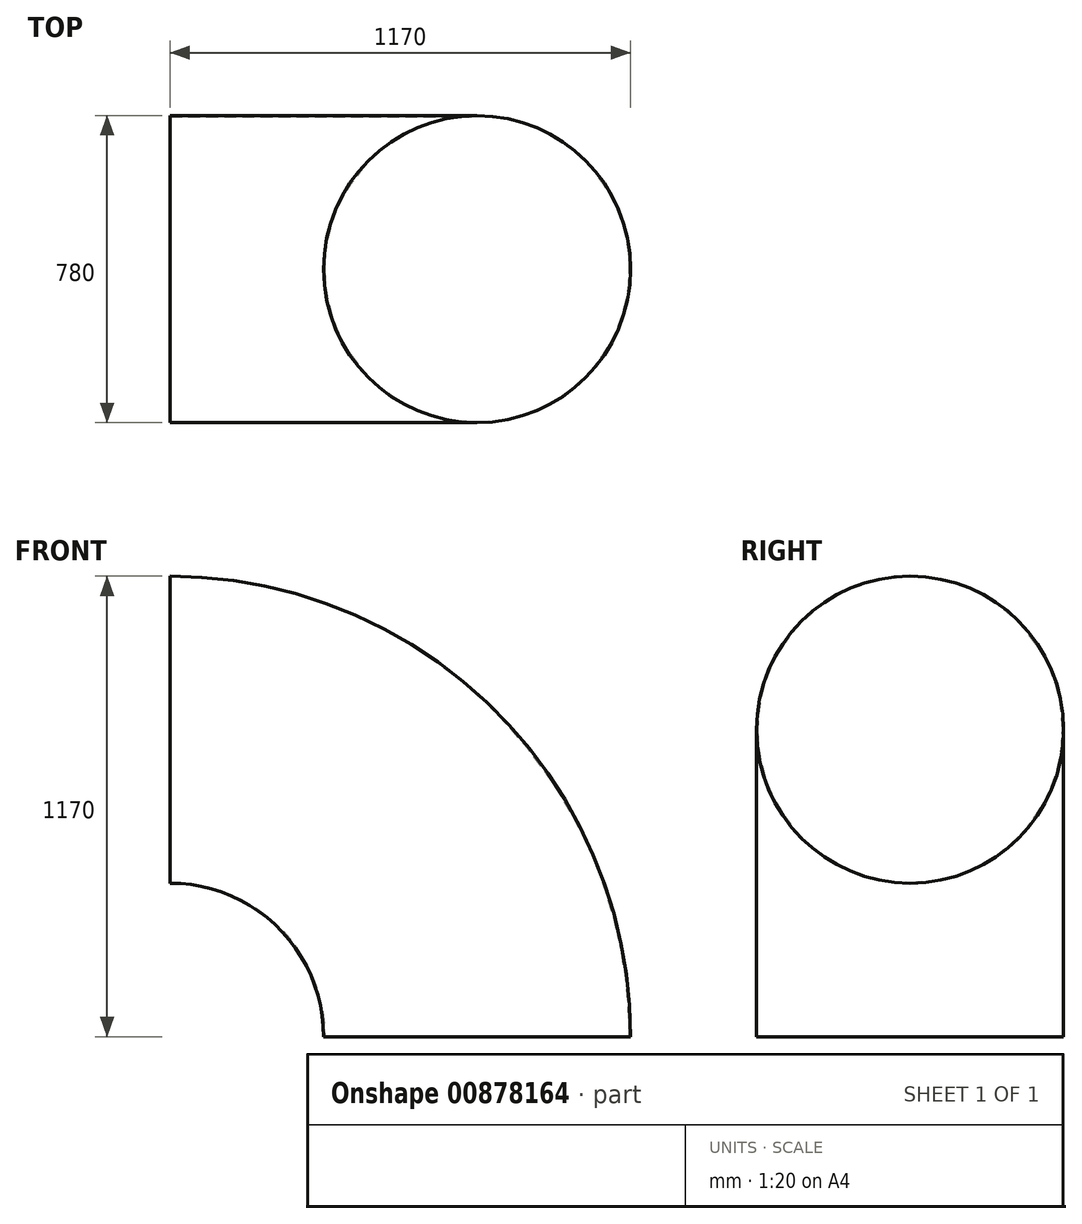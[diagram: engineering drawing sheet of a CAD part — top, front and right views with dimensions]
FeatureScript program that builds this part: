
annotation { "Feature Type Name" : "Feature", "Feature Type Description" : "" }
export const myFeature = defineFeature(function(context is Context, id is Id, definition is map)
    precondition{}
    {
        {
            var Q0;
            Q0=qCreatedBy(makeId("Front.planeOp"),FACE);
            var sketch = newSketch(context, id + "F0", { "sketchPlane" : qUnion([Q0])});
            skCircle(sketch, "E0", {"center": v(0, 0) * mm, "radius": 390 * mm, "construction": true});
            skCircle(sketch, "E1.0", {"center": v(0, 0) * mm, "radius": 1170 * mm, "construction": true});
            skArc(sketch, "E2.0", {"start": v(780, 0) * mm, "mid": v(551.54, 551.54) * mm, "end": v(0, 780) * mm});
            skPoint(sketch, "E3.start.orphan", {"position": v(966.07, 0) * mm});
            skSolve(sketch);
        }
        {
            var Q0;
            Q0=qCreatedBy(makeId("Right.planeOp"),FACE);
            var sketch = newSketch(context, id + "F1", { "sketchPlane" : qUnion([Q0])});
            skPoint(sketch, "E4.0", {"position": v(0, 780) * mm});
            skCircle(sketch, "E5", {"center": v(0, 780) * mm, "radius": 390 * mm});
            skSolve(sketch);
        }
        {
            var Q0;
            Q0=makeQuery(id+"F1.imprint","IMPRINT",FACE,{"disambiguationData":[TD([[makeQuery(id+"F1.imprint","IMPRINT",EDGE,{"derivedFrom":sQuery(id+"F1.wireOp",EDGE,"E5")}),1.0]])]});
            var Q1;
            Q1=sQuery(id+"F0.wireOp",EDGE,"E2.0");
            sweep(context, id + "F2", {"profiles" : qUnion([Q0]), "path" : qUnion([Q1])});
        }
        {
            var Q0;
            Q0=makeQuery(id+"F2.opSweep","CAP_FACE",FACE,{"disambiguationData":[OSD([sQuery(id+"F0.wireOp",VERTEX,"E2.0.end"),sQuery(id+"F1.wireOp",EDGE,"E5")])],"isStart":true});
            var Q1;
            Q1=makeQuery(id+"F2.opSweep","CAP_FACE",FACE,{"disambiguationData":[OSD([sQuery(id+"F0.wireOp",VERTEX,"E2.0.start"),sQuery(id+"F1.wireOp",EDGE,"E5")])],"isStart":false});
            shell(context, id + "F3", {"entities" : qUnion([Q0, Q1]), "thickness" : 2.3 * mm});
        }
    });
